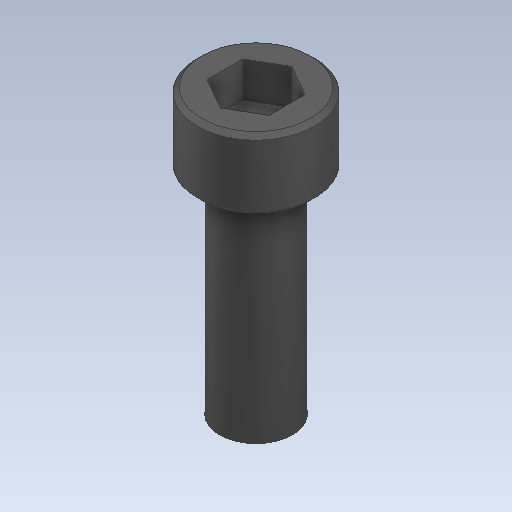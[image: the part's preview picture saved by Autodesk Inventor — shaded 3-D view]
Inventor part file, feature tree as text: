
AUTODESK INVENTOR PART (.ipt)
format: ipt  version: 2020 (Build 240168000, 168)  size: 112,128 bytes
history: native  units: in
note: dims shown in document units (in); Inventor stores cm internally (conversion verified against a paired STEP export)
features: chamfer x1
ambient origin geometry x8: Origin, YZ Plane, XZ Plane, XY Plane, X Axis, Y Axis, Z Axis, Center Point
bodies: Solid1 (feature_tree)
feature tree (1):
  chamfer  "Chamfer2"  [1 undecoded]
note: 1 required parameter value undecoded (feature->parameter linkage not recoverable at this tier; creation-order binding heuristic only, values carry confidence <= 0.55)
